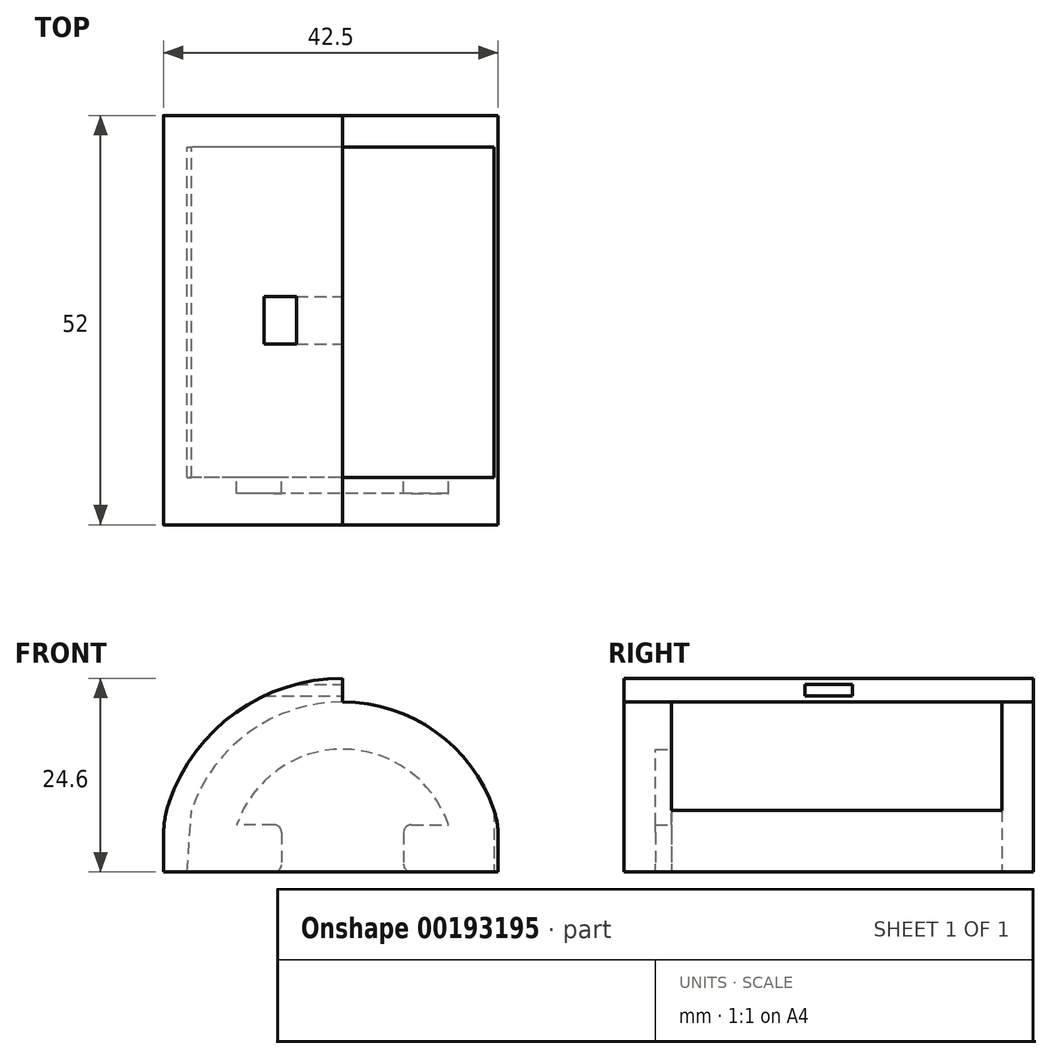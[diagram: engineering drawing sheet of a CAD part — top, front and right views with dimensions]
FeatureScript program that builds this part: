
annotation { "Feature Type Name" : "Feature", "Feature Type Description" : "" }
export const myFeature = defineFeature(function(context is Context, id is Id, definition is map)
    precondition{}
    {
        {
            var Q0;
            Q0=qCreatedBy(makeId("Front.planeOp"),FACE);
            var sketch = newSketch(context, id + "F0", { "sketchPlane" : qUnion([Q0])});
            skLineSegment(sketch, "E0", {"start": v(7.75, 0) * mm, "end": v(13.45, 0) * mm});
            skLineSegment(sketch, "E1", {"start": v(13.45, 0) * mm, "end": v(7.75, 0) * mm});
            skLineSegment(sketch, "E2", {"start": v(0, 0) * mm, "end": v(0, 9.6) * mm});
            skLineSegment(sketch, "E3", {"start": v(0, 9.6) * mm, "end": v(0, 0) * mm});
            skLineSegment(sketch, "E4", {"start": v(-7.75, 0) * mm, "end": v(-13.45, 0) * mm});
            skArc(sketch, "E5", {"start": v(13.45, 0) * mm, "mid": v(0, 9.6) * mm, "end": v(-13.45, 0) * mm});
            skLineSegment(sketch, "E6", {"start": v(-13.45, 0) * mm, "end": v(-7.75, 0) * mm});
            skLineSegment(sketch, "E7", {"start": v(-7.75, 0) * mm, "end": v(-7.75, -6) * mm});
            skLineSegment(sketch, "E8", {"start": v(-7.75, -6) * mm, "end": v(-19.75, -6) * mm});
            skLineSegment(sketch, "E9", {"start": v(-19.75, -6) * mm, "end": v(-19.75, 0) * mm});
            skLineSegment(sketch, "E10", {"start": v(7.75, 0) * mm, "end": v(7.75, -6) * mm});
            skLineSegment(sketch, "E11", {"start": v(7.75, -6) * mm, "end": v(19.75, -6) * mm});
            skLineSegment(sketch, "E12", {"start": v(19.75, -6) * mm, "end": v(19.75, 0) * mm});
            skLineSegment(sketch, "E13", {"start": v(0, 9.6) * mm, "end": v(0, 15.6) * mm});
            skArc(sketch, "E14", {"start": v(19.75, 0) * mm, "mid": v(0, 15.6) * mm, "end": v(-19.75, 0) * mm});
            skSolve(sketch);
        }
        {
            var Q0;
            Q0 = qSketchRegion(id + "F0", true);
            extrude(context, id + "F1", {"entities" : qUnion([Q0]), "endBound" : BoundingType.SYMMETRIC, "depth" : 44 * mm});
        }
        {
            var Q0;
            Q0=makeQuery(id+"F1.opExtrude","SWEPT_EDGE",EDGE,{"disambiguationData":[OSD([sQuery(id+"F0.wireOp",EDGE,"E7"),sQuery(id+"F0.wireOp",EDGE,"E8")])]});
            var Q1;
            Q1=makeQuery(id+"F1.opExtrude","SWEPT_EDGE",EDGE,{"disambiguationData":[OSD([sQuery(id+"F0.wireOp",EDGE,"E6"),sQuery(id+"F0.wireOp",EDGE,"E7")])]});
            var Q2;
            Q2=makeQuery(id+"F1.opExtrude","SWEPT_EDGE",EDGE,{"disambiguationData":[OSD([sQuery(id+"F0.wireOp",EDGE,"E1"),sQuery(id+"F0.wireOp",EDGE,"E10")])]});
            var Q3;
            Q3=makeQuery(id+"F1.opExtrude","SWEPT_EDGE",EDGE,{"disambiguationData":[OSD([sQuery(id+"F0.wireOp",EDGE,"E10"),sQuery(id+"F0.wireOp",EDGE,"E11")])]});
            fillet(context, id + "F10", {"entities" : qUnion([Q0, Q1, Q2, Q3]), "radius" : 1 * mm, "tangentPropagation" : true, "allowEdgeOverflow" : false});
        }
        {
            var Q0;
            Q0=makeQuery(id+"F1.opExtrude","SWEPT_EDGE",EDGE,{"disambiguationData":[OSD([sQuery(id+"F0.wireOp",EDGE,"E12"),sQuery(id+"F0.wireOp",EDGE,"E14")])]});
            var Q1;
            Q1=makeQuery(id+"F1.opExtrude","SWEPT_EDGE",EDGE,{"disambiguationData":[OSD([sQuery(id+"F0.wireOp",EDGE,"E9"),sQuery(id+"F0.wireOp",EDGE,"E14")])]});
            fillet(context, id + "F11", {"entities" : qUnion([Q0, Q1]), "radius" : 10 * mm, "tangentPropagation" : true, "allowEdgeOverflow" : false});
        }
        {
            var Q0;
            Q0=makeQuery(id+"F1.opExtrude","CAP_FACE",FACE,{"disambiguationData":[OSD([sQuery(id+"F0.wireOp",EDGE,"E5"),sQuery(id+"F0.wireOp",EDGE,"E6"),sQuery(id+"F0.wireOp",EDGE,"E7"),sQuery(id+"F0.wireOp",EDGE,"E8"),sQuery(id+"F0.wireOp",EDGE,"E9"),sQuery(id+"F0.wireOp",EDGE,"E1"),sQuery(id+"F0.wireOp",EDGE,"E10"),sQuery(id+"F0.wireOp",EDGE,"E11"),sQuery(id+"F0.wireOp",EDGE,"E12"),sQuery(id+"F0.wireOp",EDGE,"E14")])],"isStart":false});
            var sketch = newSketch(context, id + "F2", { "sketchPlane" : qUnion([Q0])});
            skArc(sketch, "E15.0", {"start": v(19.21, 1.85) * mm, "mid": v(0, 15.6) * mm, "end": v(-19.21, 1.85) * mm});
            skPoint(sketch, "E16.0", {"position": v(-19.75, -6) * mm});
            skPoint(sketch, "E17.0", {"position": v(-19.75, -1.38) * mm});
            skLineSegment(sketch, "E18.0", {"start": v(-8.75, -6) * mm, "end": v(-19.75, -6) * mm});
            skLineSegment(sketch, "E19.0", {"start": v(-19.75, -6) * mm, "end": v(-19.75, -1.38) * mm});
            skArc(sketch, "E20.0", {"start": v(-19.21, 1.85) * mm, "mid": v(-19.62, 0.26) * mm, "end": v(-19.75, -1.38) * mm});
            skArc(sketch, "E21.0", {"start": v(19.75, -1.38) * mm, "mid": v(19.62, 0.26) * mm, "end": v(19.21, 1.85) * mm});
            skLineSegment(sketch, "E22.0", {"start": v(19.75, -6) * mm, "end": v(19.75, -1.38) * mm});
            skLineSegment(sketch, "E23.0", {"start": v(8.75, -6) * mm, "end": v(19.75, -6) * mm});
            skLineSegment(sketch, "E24", {"start": v(8.75, -6) * mm, "end": v(-8.75, -6) * mm});
            skSolve(sketch);
        }
        {
            var Q0;
            Q0 = qSketchRegion(id + "F2", true);
            extrude(context, id + "F3", {"entities" : qUnion([Q0]), "depth" : 4 * mm});
        }
        {
            var Q0;
            Q0=makeQuery(id+"F3.opExtrude","SWEPT_BODY",BODY,{"disambiguationData":[OSD([sQuery(id+"F2.wireOp",EDGE,"E15.0"),sQuery(id+"F2.wireOp",EDGE,"E18.0"),sQuery(id+"F2.wireOp",EDGE,"E19.0"),sQuery(id+"F2.wireOp",EDGE,"E20.0"),sQuery(id+"F2.wireOp",EDGE,"E21.0"),sQuery(id+"F2.wireOp",EDGE,"E22.0"),sQuery(id+"F2.wireOp",EDGE,"E23.0"),sQuery(id+"F2.wireOp",EDGE,"E24")])]});
            var Q1;
            Q1=qCreatedBy(makeId("Front.planeOp"),FACE);
            mirror(context, id + "F12", {"entities" : qUnion([Q0]), "mirrorPlane" : qUnion([Q1])});
        }
        {
            var Q0;
            Q0=makeQuery(id+"F12.opPattern","COPY",FACE,{"derivedFrom":makeQuery(id+"F3.opExtrude","CAP_FACE",FACE,{"disambiguationData":[OSD([sQuery(id+"F2.wireOp",EDGE,"E15.0"),sQuery(id+"F2.wireOp",EDGE,"E18.0"),sQuery(id+"F2.wireOp",EDGE,"E19.0"),sQuery(id+"F2.wireOp",EDGE,"E20.0"),sQuery(id+"F2.wireOp",EDGE,"E21.0"),sQuery(id+"F2.wireOp",EDGE,"E22.0"),sQuery(id+"F2.wireOp",EDGE,"E23.0"),sQuery(id+"F2.wireOp",EDGE,"E24")])],"isStart":true}),"instanceName":"1"});
            var sketch = newSketch(context, id + "F4", { "sketchPlane" : qUnion([Q0])});
            skArc(sketch, "E25.0", {"start": v(19.21, 1.85) * mm, "mid": v(0, 15.6) * mm, "end": v(-19.21, 1.85) * mm});
            skLineSegment(sketch, "E26", {"start": v(19.21, 1.85) * mm, "end": v(19.21, -6) * mm});
            skLineSegment(sketch, "E27", {"start": v(-19.75, -6) * mm, "end": v(19.21, -6) * mm});
            skLineSegment(sketch, "E28", {"start": v(-19.75, -6) * mm, "end": v(-19.21, 1.85) * mm});
            skSolve(sketch);
        }
        {
            var Q0;
            Q0 = qSketchRegion(id + "F4", true);
            extrude(context, id + "F5", {"entities" : qUnion([Q0]), "operationType" : NewBodyOperationType.REMOVE, "depth" : 42 * mm});
        }
        {
            var Q0;
            Q0=makeQuery(id+"F3.opExtrude","CAP_FACE",FACE,{"disambiguationData":[OSD([sQuery(id+"F2.wireOp",EDGE,"E15.0"),sQuery(id+"F2.wireOp",EDGE,"E18.0"),sQuery(id+"F2.wireOp",EDGE,"E19.0"),sQuery(id+"F2.wireOp",EDGE,"E20.0"),sQuery(id+"F2.wireOp",EDGE,"E21.0"),sQuery(id+"F2.wireOp",EDGE,"E22.0"),sQuery(id+"F2.wireOp",EDGE,"E23.0"),sQuery(id+"F2.wireOp",EDGE,"E24")])],"isStart":false});
            var sketch = newSketch(context, id + "F6", { "sketchPlane" : qUnion([Q0])});
            skArc(sketch, "E29.0", {"start": v(-22.05, 2.82) * mm, "mid": v(-22.57, 0.75) * mm, "end": v(-22.75, -1.38) * mm});
            skLineSegment(sketch, "E29.3", {"start": v(-22.75, -1.38) * mm, "end": v(-22.75, -6) * mm});
            skArc(sketch, "E30", {"start": v(0, 18.6) * mm, "mid": v(-13.56, 14.25) * mm, "end": v(-22.05, 2.82) * mm});
            skLineSegment(sketch, "E31.0", {"start": v(-19.75, -6) * mm, "end": v(-19.75, -1.38) * mm});
            skArc(sketch, "E32.0", {"start": v(-19.21, 1.85) * mm, "mid": v(-19.62, 0.26) * mm, "end": v(-19.75, -1.38) * mm});
            skArc(sketch, "E33.0", {"start": v(0, 15.6) * mm, "mid": v(-11.81, 11.8) * mm, "end": v(-19.21, 1.85) * mm});
            skLineSegment(sketch, "E34", {"start": v(0, 18.6) * mm, "end": v(0, 15.6) * mm});
            skPoint(sketch, "E35.orphan", {"position": v(19.21, 1.85) * mm});
            skLineSegment(sketch, "E36", {"start": v(-19.75, -6) * mm, "end": v(-22.75, -6) * mm});
            skPoint(sketch, "E37.end.orphan", {"position": v(-19.75, -9) * mm});
            skSolve(sketch);
        }
        {
            var Q0;
            Q0 = qSketchRegion(id + "F6", true);
            var Q1;
            Q1=makeQuery(id+"F12.opPattern","COPY",FACE,{"derivedFrom":makeQuery(id+"F3.opExtrude","CAP_FACE",FACE,{"disambiguationData":[OSD([sQuery(id+"F2.wireOp",EDGE,"E15.0"),sQuery(id+"F2.wireOp",EDGE,"E18.0"),sQuery(id+"F2.wireOp",EDGE,"E19.0"),sQuery(id+"F2.wireOp",EDGE,"E20.0"),sQuery(id+"F2.wireOp",EDGE,"E21.0"),sQuery(id+"F2.wireOp",EDGE,"E22.0"),sQuery(id+"F2.wireOp",EDGE,"E23.0"),sQuery(id+"F2.wireOp",EDGE,"E24")])],"isStart":false}),"instanceName":"1"});
            extrude(context, id + "F7", {"entities" : qUnion([Q0]), "operationType" : NewBodyOperationType.ADD, "endBound" : BoundingType.UP_TO_SURFACE, "oppositeDirection" : true, "endBoundEntityFace" : qUnion([Q1]), "depth" : 50 * mm});
        }
        {
            var Q0;
            Q0=makeQuery(id+"F7.opExtrude","SWEPT_FACE",FACE,{"disambiguationData":[OSD([sQuery(id+"F6.wireOp",EDGE,"E34")])]});
            var sketch = newSketch(context, id + "F8", { "sketchPlane" : qUnion([Q0])});
            skLineSegment(sketch, "E38", {"start": v(0, 18.6) * mm, "end": v(0, 15.6) * mm, "construction": true});
            skLineSegment(sketch, "E39.bottom", {"start": v(3, 16.35) * mm, "end": v(-3, 16.35) * mm});
            skLineSegment(sketch, "E39.top", {"start": v(3, 17.85) * mm, "end": v(-3, 17.85) * mm});
            skLineSegment(sketch, "E39.left", {"start": v(3, 16.35) * mm, "end": v(3, 17.85) * mm});
            skLineSegment(sketch, "E39.right", {"start": v(-3, 16.35) * mm, "end": v(-3, 17.85) * mm});
            skPoint(sketch, "E39.middle", {"position": v(0, 17.1) * mm});
            skSolve(sketch);
        }
        {
            var Q0;
            Q0 = qSketchRegion(id + "F8", true);
            var Q1;
            Q1=sQuery(id+"F8.wireOp",EDGE,"mAqm9zfH-Acyj-6Nde-obMa-DQJZb48d4oos");
            extrude(context, id + "F9", {"entities" : qUnion([Q0]), "operationType" : NewBodyOperationType.REMOVE, "surfaceEntities" : qUnion([Q1]), "oppositeDirection" : true, "depth" : 25 * mm});
        }
    });
